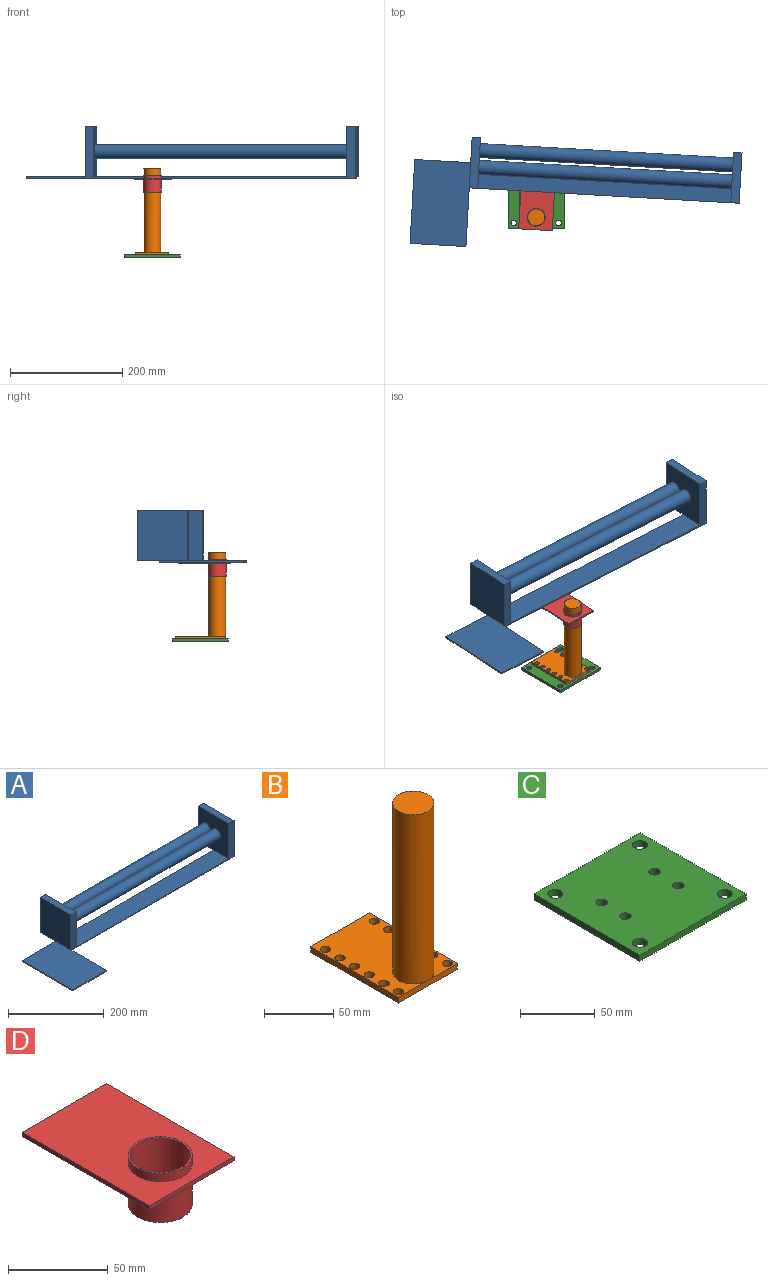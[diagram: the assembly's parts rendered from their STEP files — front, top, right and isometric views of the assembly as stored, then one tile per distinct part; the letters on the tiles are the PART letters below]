
ASSEMBLY  parts=4 mates=4
PART A: 20 faces, bbox 582.6x195x92.5 mm
  f0: plane 452.6x45mm, normal (0,0,1), area 20367mm2, adj f2,f4,f10,f14
  f1: plane 150x100mm, normal (0,0,1), area 15000mm2, adj f4,f5,f6,f7,f9
  f2: plane 482.6x92.5mm, normal (0,-1,0), area 3906.5mm2, adj f0,f3,f7,f8,f9,f10,f12,f14
  f3: plane 92.5x90mm, normal (1,0,0), area 8212.5mm2, adj f2,f4,f8,f15,f16,f17
  f4: plane 582.6x2.5mm, normal (0,1,0), area 1456.5mm2, adj f0,f1,f3,f5,f8,f13,f17
  f5: plane 150x2.5mm, normal (-1,0,0), area 375mm2, adj f1,f4,f6,f8
  f6: plane 100x2.5mm, normal (0,-1,0), area 250mm2, adj f1,f5,f7,f8
  f7: plane 105x2.5mm, normal (1,0,0), area 262.5mm2, adj f1,f2,f6,f8
  f8: plane 582.6x150mm, normal (0,0,-1), area 36717mm2, adj f2,f3,f4,f5,f6,f7
  f9: plane 90x90mm, normal (-1,0,0), area 8100mm2, adj f1,f2,f11,f12,f13
  f10: plane 90x90mm, normal (1,0,0), area 7118.3mm2, adj f0,f2,f11,f12,f13,f18,f19
  f11: plane 90x15mm, normal (0,1,0), area 1350mm2, adj f9,f10,f12,f13
  f12: plane 90x15mm, normal (0,0,1), area 1350mm2, adj f2,f9,f10,f11
  f13: plane 45x15mm, normal (0,0,-1), area 675mm2, adj f4,f9,f10,f11
  f14: plane 90x90mm, normal (-1,0,0), area 7118.3mm2, adj f0,f2,f15,f16,f17,f18,f19
  f15: plane 90x15mm, normal (0,1,0), area 1350mm2, adj f3,f14,f16,f17
  f16: plane 90x15mm, normal (0,0,1), area 1350mm2, adj f2,f3,f14,f15
  f17: plane 45x15mm, normal (0,0,-1), area 675mm2, adj f3,f4,f14,f15
  f18: cylinder r=12.5mm len=452.6mm, axis (-1,0,0), area 35547.1mm2, adj f10,f14
  f19: cylinder r=12.5mm len=452.6mm, axis (-1,0,0), area 35547.1mm2, adj f10,f14
PART B: 20 faces, bbox 60x90x155 mm
  f0: cylinder r=15mm len=150mm, axis (0,0,1), area 14137.2mm2, adj f1,f19
  f1: plane 30x30mm, normal (0,0,1), area 706.9mm2, adj f0
  f2: plane 90x5mm, normal (1,0,0), area 450mm2, adj f3,f17,f18,f19
  f3: plane 60x5mm, normal (0,-1,0), area 300mm2, adj f2,f4,f18,f19
  f4: plane 90x5mm, normal (-1,0,0), area 450mm2, adj f3,f17,f18,f19
  f5: cylinder r=3.75mm len=7.5mm, axis (0,0,1), area 117.8mm2, adj f18,f19
  f6: cylinder r=3.75mm len=7.5mm, axis (0,0,1), area 117.8mm2, adj f18,f19
  f7: cylinder r=3.75mm len=7.5mm, axis (0,0,1), area 117.8mm2, adj f18,f19
  f8: cylinder r=3.75mm len=7.5mm, axis (0,0,1), area 117.8mm2, adj f18,f19
  f9: cylinder r=3.75mm len=7.5mm, axis (0,0,1), area 117.8mm2, adj f18,f19
  f10: cylinder r=3.75mm len=7.5mm, axis (0,0,1), area 117.8mm2, adj f18,f19
  f11: cylinder r=3.75mm len=7.5mm, axis (0,0,1), area 117.8mm2, adj f18,f19
  f12: cylinder r=3.75mm len=7.5mm, axis (0,0,1), area 117.8mm2, adj f18,f19
  f13: cylinder r=3.75mm len=7.5mm, axis (0,0,1), area 117.8mm2, adj f18,f19
  f14: cylinder r=3.75mm len=7.5mm, axis (0,0,1), area 117.8mm2, adj f18,f19
  f15: cylinder r=3.75mm len=7.5mm, axis (0,0,1), area 117.8mm2, adj f18,f19
  f16: cylinder r=3.75mm len=7.5mm, axis (0,0,1), area 117.8mm2, adj f18,f19
  f17: plane 60x5mm, normal (0,1,0), area 300mm2, adj f2,f4,f18,f19
  f18: plane 90x60mm, normal (0,0,-1), area 4869.9mm2, adj f2,f3,f4,f5,f6,f7,f8,f9
  f19: plane 90x60mm, normal (0,0,1), area 4163mm2, adj f0,f2,f3,f4,f5,f6,f7,f8
PART C: 14 faces, bbox 100x100x5 mm
  f0: plane 100x5mm, normal (0,1,0), area 500mm2, adj f1,f11,f12,f13
  f1: plane 100x5mm, normal (-1,0,0), area 500mm2, adj f0,f2,f12,f13
  f2: plane 100x5mm, normal (0,-1,0), area 500mm2, adj f1,f11,f12,f13
  f3: cylinder r=3.75mm len=7.5mm, axis (0,0,-1), area 117.8mm2, adj f12,f13
  f4: cylinder r=3.75mm len=7.5mm, axis (0,0,-1), area 117.8mm2, adj f12,f13
  f5: cylinder r=3.75mm len=7.5mm, axis (0,0,-1), area 117.8mm2, adj f12,f13
  f6: cylinder r=5mm len=10mm, axis (0,0,-1), area 157.1mm2, adj f12,f13
  f7: cylinder r=5mm len=10mm, axis (0,0,-1), area 157.1mm2, adj f12,f13
  f8: cylinder r=5mm len=10mm, axis (0,0,-1), area 157.1mm2, adj f12,f13
  f9: cylinder r=5mm len=10mm, axis (0,0,-1), area 157.1mm2, adj f12,f13
  f10: cylinder r=3.75mm len=7.5mm, axis (0,0,-1), area 117.8mm2, adj f12,f13
  f11: plane 100x5mm, normal (1,0,0), area 500mm2, adj f0,f2,f12,f13
  f12: plane 100x100mm, normal (0,0,1), area 9509.1mm2, adj f0,f1,f2,f3,f4,f5,f6,f7
  f13: plane 100x100mm, normal (0,0,-1), area 9509.1mm2, adj f0,f1,f2,f3,f4,f5,f6,f7
PART D: 11 faces, bbox 60x90x30 mm
  f0: plane 60x2.5mm, normal (0,1,0), area 150mm2, adj f1,f4,f5,f6
  f1: plane 90x2.5mm, normal (-1,0,0), area 225mm2, adj f0,f2,f5,f6
  f2: plane 60x2.5mm, normal (0,-1,0), area 150mm2, adj f1,f4,f5,f6
  f3: cylinder r=15mm len=30mm, axis (0,0,-1), area 2827.4mm2, adj f8,f10
  f4: plane 90x2.5mm, normal (1,0,0), area 225mm2, adj f0,f2,f5,f6
  f5: plane 90x60mm, normal (0,0,1), area 4595.8mm2, adj f0,f1,f2,f4,f7
  f6: plane 90x60mm, normal (0,0,-1), area 4595.8mm2, adj f0,f1,f2,f4,f9
  f7: cylinder r=16mm len=32mm, axis (0,0,-1), area 502.7mm2, adj f5,f8
  f8: plane 32x32mm, normal (0,0,1), area 97.4mm2, adj f3,f7
  f9: cylinder r=16mm len=32mm, axis (0,0,1), area 2261.9mm2, adj f6,f10
  f10: plane 32x32mm, normal (0,0,-1), area 97.4mm2, adj f3,f9
PLACE A rot(axis=(0,0,-1),3.3deg) t=(76.26,15.42,75.77)mm
PLACE B t=(-548.43,-3.51,93.71)mm
PLACE C t=(-993.4,26.76,-66.29)mm fixed
PLACE D rot(axis=(0,0,-1),3.3deg) t=(-40.39,60.06,73.27)mm
MATE planar C.f12 <-> B.f18  axis (0,0,1) through (-46.45,-15.74,-61.29)mm
MATE fastened B.f18 <-> C.f12  axis (0,0,-1) through (-46.45,-15.74,-61.29)mm
MATE fastened D.f5 <-> A.f8  axis (0,0,1) through (-44.91,-19.18,75.77)mm
MATE cylindrical B.f0 <-> D.f3  axis (0,0,1) through (-46.45,-46.01,18.71)mm
